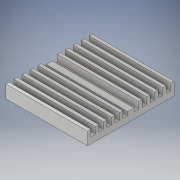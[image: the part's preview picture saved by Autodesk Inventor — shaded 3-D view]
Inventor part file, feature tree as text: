
AUTODESK INVENTOR PART (.ipt)
format: ipt  version: 2019.2 (Build 232265000, 265)  size: 169,984 bytes
history: native  units: mm
features: extrude x2, sketch x1
ambient origin geometry x8: Origin, YZ Plane, XZ Plane, XY Plane, X Axis, Y Axis, Z Axis, Center Point
bodies: Solid1 (feature_tree)
feature tree (3):
  extrude  "Extrusion1"  Depth=27.0mm
  extrude  "Extrusion3"  Depth=4.0mm TaperAngle=0.0deg
  sketch  "Sketch1"  dims[d0=25.5mm d1=27.0mm d2=4.0mm d3=0.0mm d5=1.0mm d6=1.5mm d7=1.5mm d8=1.0mm d9=1.5mm d10=1.0mm d12=2.0mm d13=1.5mm d14=1.0mm d17=1.5mm d18=1.0mm d19=10.0mm d20=0.0mm]
